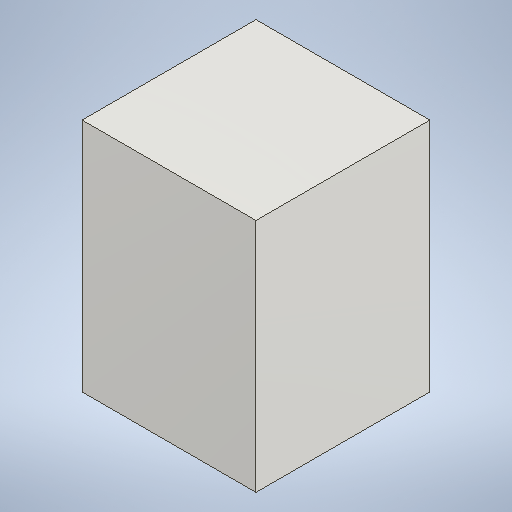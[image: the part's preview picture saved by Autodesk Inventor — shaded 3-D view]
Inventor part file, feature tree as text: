
AUTODESK INVENTOR PART (.ipt)
format: ipt  version: 2025 (Build 290162000, 162)  size: 219,648 bytes
history: native  units: in
note: dims shown in document units (in); Inventor stores cm internally (conversion verified against a paired STEP export)
features: extrude x1, sketch x1
ambient origin geometry x8: Origin, YZ Plane, XZ Plane, XY Plane, X Axis, Y Axis, Z Axis, Center Point
bodies: Solid1 (feature_tree)
feature tree (2):
  extrude  "Extrusion1"  Depth=24.0in
  sketch  "Sketch1"  dims[d2=32.5in d3=0.0in d6=24.0in d8=24.0in]
